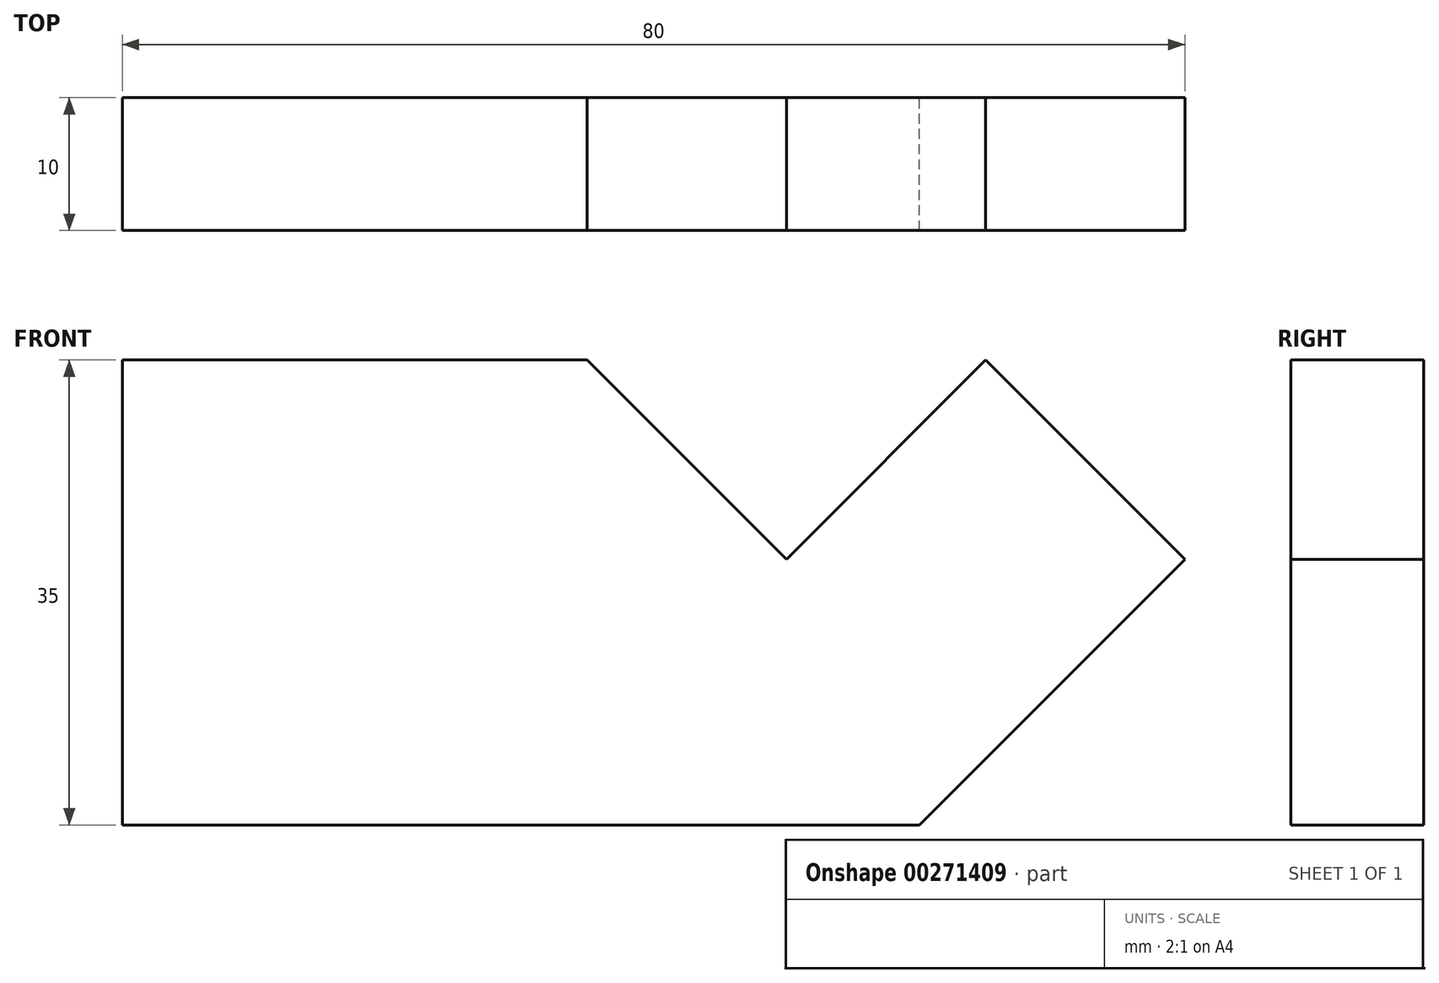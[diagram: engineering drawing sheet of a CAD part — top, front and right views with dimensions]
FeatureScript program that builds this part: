
annotation { "Feature Type Name" : "Feature", "Feature Type Description" : "" }
export const myFeature = defineFeature(function(context is Context, id is Id, definition is map)
    precondition{}
    {
        {
            var Q0;
            Q0=qCreatedBy(makeId("Front.planeOp"),FACE);
            var sketch = newSketch(context, id + "F0", { "sketchPlane" : qUnion([Q0])});
            skLineSegment(sketch, "E0", {"start": v(0, 0) * mm, "end": v(60, 0) * mm});
            skLineSegment(sketch, "E1", {"start": v(80, 20) * mm, "end": v(60, 0) * mm});
            skLineSegment(sketch, "E2", {"start": v(80, 20) * mm, "end": v(65, 35) * mm});
            skLineSegment(sketch, "E3", {"start": v(65, 35) * mm, "end": v(50, 20) * mm});
            skLineSegment(sketch, "E4", {"start": v(50, 20) * mm, "end": v(35, 35) * mm});
            skLineSegment(sketch, "E5", {"start": v(35, 35) * mm, "end": v(0, 35) * mm});
            skLineSegment(sketch, "E6", {"start": v(0, 35) * mm, "end": v(0, 0) * mm});
            skSolve(sketch);
        }
        {
            var Q0;
            Q0=makeQuery(id+"F0.imprint","IMPRINT",FACE,{"disambiguationData":[TD([[makeQuery(id+"F0.imprint","IMPRINT",EDGE,{"derivedFrom":sQuery(id+"F0.wireOp",EDGE,"E0")}),1.0]])]});
            extrude(context, id + "F1", {"entities" : qUnion([Q0]), "depth" : 10 * mm});
        }
    });
